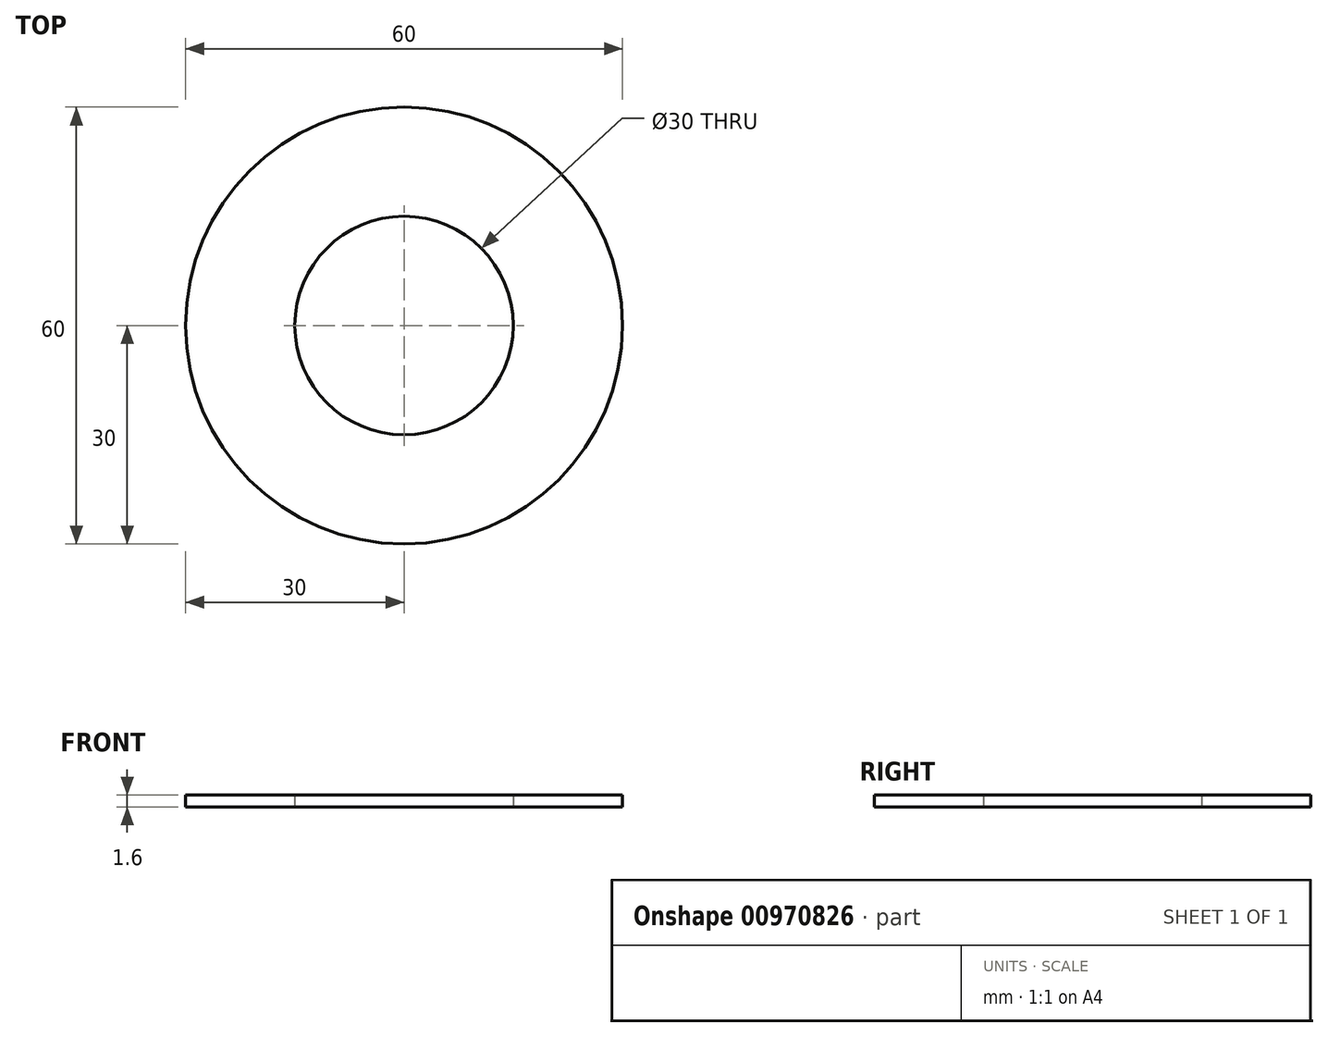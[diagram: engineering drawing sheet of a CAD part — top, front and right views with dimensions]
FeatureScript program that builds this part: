
annotation { "Feature Type Name" : "Feature", "Feature Type Description" : "" }
export const myFeature = defineFeature(function(context is Context, id is Id, definition is map)
    precondition{}
    {
        {
            var Q0;
            Q0=qCreatedBy(makeId("Top.planeOp"),FACE);
            var sketch = newSketch(context, id + "F0", { "sketchPlane" : qUnion([Q0])});
            skLineSegment(sketch, "E0.bottom", {"start": v(0, 0) * mm, "end": v(60, 0) * mm});
            skLineSegment(sketch, "E0.top", {"start": v(0, -60) * mm, "end": v(60, -60) * mm});
            skLineSegment(sketch, "E0.left", {"start": v(0, 0) * mm, "end": v(0, -60) * mm});
            skLineSegment(sketch, "E0.right", {"start": v(60, 0) * mm, "end": v(60, -60) * mm});
            skLineSegment(sketch, "E1", {"start": v(0, 0) * mm, "end": v(60, -60) * mm});
            skCircle(sketch, "E2", {"center": v(30, -30) * mm, "radius": 15 * mm});
            skCircle(sketch, "E3", {"center": v(30, -30) * mm, "radius": 30 * mm});
            skSolve(sketch);
        }
        {
            var Q0;
            {var subQ0=sQuery(id+"F0.wireOp",EDGE,"E3");var subQ2=sQuery(id+"F0.wireOp",EDGE,"E1");var subQ3=makeQuery(id+"F0.imprint","INTERSECT",VERTEX,{"disambiguationData":[OD(0.0)],"derivedFrom":[subQ2,subQ0]});Q0=makeQuery(id+"F0.imprint","IMPRINT",FACE,{"disambiguationData":[TD([[makeQuery(id+"F0.imprint","IMPRINT",EDGE,{"disambiguationData":[TD([[subQ3,-1.0]])],"derivedFrom":subQ2}),-1.0]])]});}
            var Q1;
            {var subQ0=sQuery(id+"F0.wireOp",EDGE,"E3");var subQ4=sQuery(id+"F0.wireOp",EDGE,"E1");var subQ8=makeQuery(id+"F0.imprint","INTERSECT",VERTEX,{"disambiguationData":[OD(0.0)],"derivedFrom":[subQ4,subQ0]});Q1=makeQuery(id+"F0.imprint","IMPRINT",FACE,{"disambiguationData":[TD([[makeQuery(id+"F0.imprint","IMPRINT",EDGE,{"disambiguationData":[TD([[subQ8,-1.0]])],"derivedFrom":subQ4}),1.0]])]});}
            extrude(context, id + "F1", {"entities" : qUnion([Q0, Q1]), "depth" : 1.6 * mm, "offsetDistance" : 25 * mm});
        }
    });
